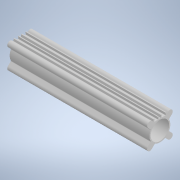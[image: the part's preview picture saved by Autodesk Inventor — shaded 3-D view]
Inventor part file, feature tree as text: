
AUTODESK INVENTOR PART (.ipt)
format: ipt  version: 2024.3 (Build 283343000, 343)  size: 215,552 bytes
history: native  units: mm
features: other x49, extrude x1, sketch x1
ambient origin geometry x8: Origin, YZ Plane, XZ Plane, XY Plane, X Axis, Y Axis, Z Axis, Center Point
bodies: Solid1 (feature_tree)
feature tree (51):
  extrude  "Extrusion1"  TaperAngle=0.0deg  [1 undecoded]
  other  "br_l_XY"
  other  "br_l_YZ"
  other  "br_l_ZX"
  other  "br_l_X"
  other  "br_l_Y"
  other  "br_l_Z"
  other  "br_l_Center"
  other  "br_r_XY"
  other  "br_r_YZ"
  other  "br_r_ZX"
  other  "br_r_X"
  other  "br_r_Y"
  other  "br_r_Z"
  other  "br_r_Center"
  other  "mod_en_XY"
  other  "mod_en_YZ"
  other  "mod_en_ZX"
  other  "mod_en_X"
  other  "mod_en_Y"
  other  "mod_en_Z"
  other  "mod_en_Center"
  other  "sens_sqr_l_XY"
  other  "sens_sqr_l_YZ"
  other  "sens_sqr_l_ZX"
  other  "sens_sqr_l_X"
  other  "sens_sqr_l_Y"
  other  "sens_sqr_l_Z"
  other  "sens_sqr_l_Center"
  other  "sens_sqr_r_XY"
  other  "sens_sqr_r_YZ"
  other  "sens_sqr_r_ZX"
  other  "sens_sqr_r_X"
  other  "sens_sqr_r_Y"
  other  "sens_sqr_r_Z"
  other  "sens_sqr_r_Center"
  other  "sensor_l_XY"
  other  "sensor_l_YZ"
  other  "sensor_l_ZX"
  other  "sensor_l_X"
  other  "sensor_l_Y"
  other  "sensor_l_Z"
  other  "sensor_l_Center"
  other  "sensor_r_XY"
  other  "sensor_r_YZ"
  other  "sensor_r_ZX"
  other  "sensor_r_X"
  other  "sensor_r_Y"
  other  "sensor_r_Z"
  other  "sensor_r_Center"
  sketch  "Sketch_1"  dims[d0=242.0mm d1=0.0mm d2=0.0mm d3=0.0mm d4=0.0mm d5=0.0mm]
note: 1 required parameter value undecoded (feature->parameter linkage not recoverable at this tier; creation-order binding heuristic only, values carry confidence <= 0.55)
